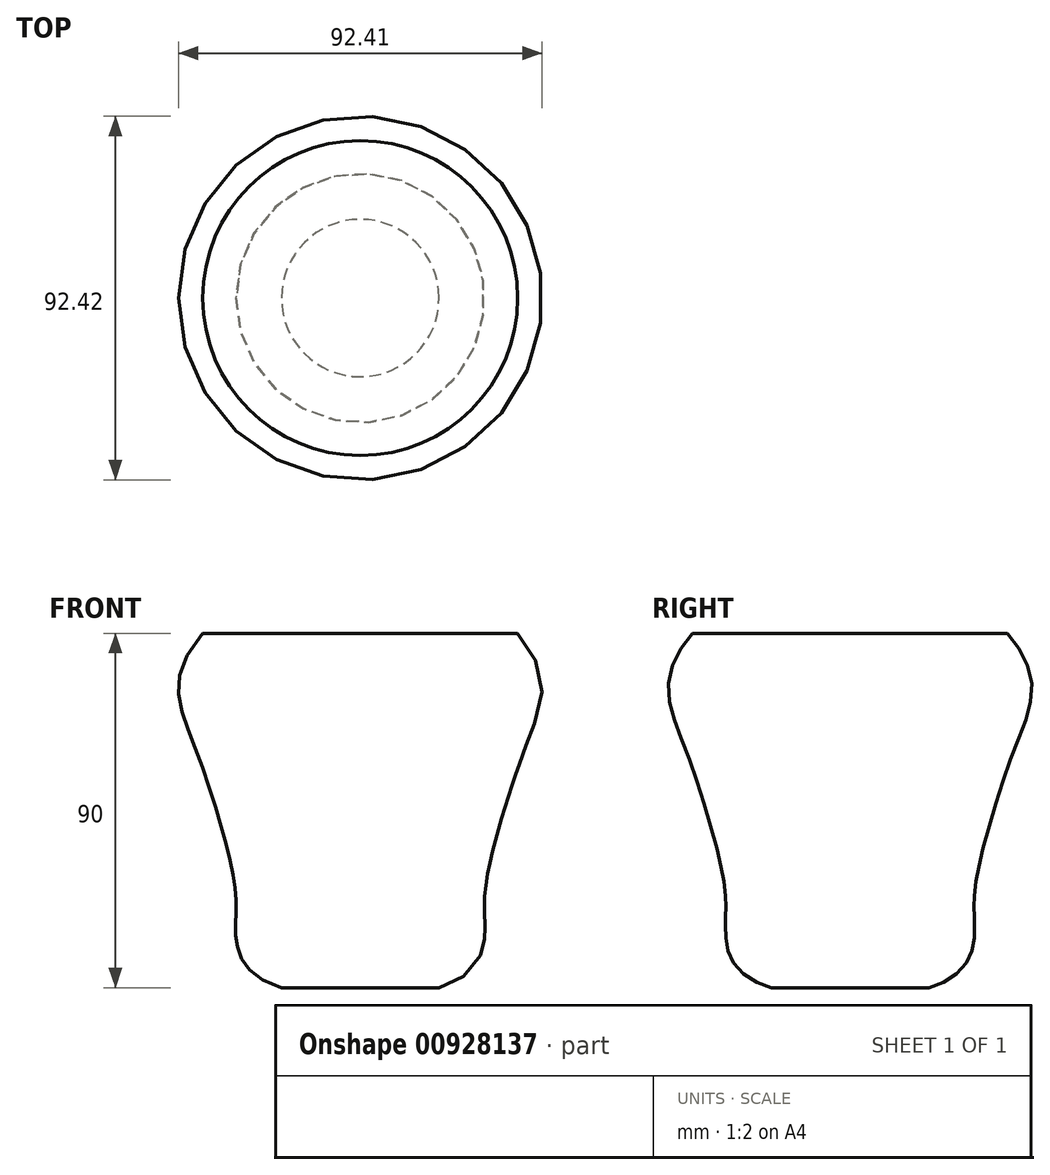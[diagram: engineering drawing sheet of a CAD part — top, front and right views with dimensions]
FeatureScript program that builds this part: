
annotation { "Feature Type Name" : "Feature", "Feature Type Description" : "" }
export const myFeature = defineFeature(function(context is Context, id is Id, definition is map)
    precondition{}
    {
        {
            var Q0;
            Q0=qCreatedBy(makeId("Right.planeOp"),FACE);
            var sketch = newSketch(context, id + "F0", { "sketchPlane" : qUnion([Q0])});
            skLineSegment(sketch, "E0", {"start": v(0, 90) * mm, "end": v(0, 0) * mm});
            skLineSegment(sketch, "E1", {"start": v(0, 90) * mm, "end": v(40, 90) * mm});
            skLineSegment(sketch, "E2", {"start": v(0, 0) * mm, "end": v(20, 0) * mm});
            skFitSpline(sketch, "E3", {"points": [v(40, 90) * mm, v(42.68, 62.9) * mm, v(33.7, 34.88) * mm, v(31.54, 21.05) * mm, v(31.36, 11.16) * mm, v(20, 0) * mm], "startDerivative": vector(118.55, -137.71) * mm, "endDerivative": vector(-132.3, -38.61) * mm});
            skPoint(sketch, "E4.1.internal.orphan", {"position": v(25.79, 21.05) * mm});
            skLineSegment(sketch, "E5", {"start": v(0, -25.61) * mm, "end": v(0, 116.5) * mm, "construction": true});
            skSolve(sketch);
        }
        {
            var Q0;
            Q0=makeQuery(id+"F0.imprint","IMPRINT",FACE,{"disambiguationData":[TD([[makeQuery(id+"F0.imprint","IMPRINT",EDGE,{"derivedFrom":sQuery(id+"F0.wireOp",EDGE,"E0")}),1.0]])]});
            var Q1;
            Q1=sQuery(id+"F0.wireOp",EDGE,"E5");
            revolve(context, id + "F1", {"surfaceOperationType" : NewSurfaceOperationType.NEW, "entities" : qUnion([Q0]), "axis" : qUnion([Q1]), "revolveType" : RevolveType.FULL});
        }
    });
